# Revit family: FantiniCosmi_BIM_AP19981
name_source: partatom
category: Generic Models
units: mm (PartAtom-declared; Revit-internal decimal feet)

## family parameters
Always vertical = Yes
Can host rebar = No
Cut with Voids When Loaded = No
Part Type = Normal
Room Calculation Point = No
Round Connector Dimension = Use Diameter
Shared = No
Work Plane-Based = No

## types (1)
- Standard
    Default Elevation = 0 mm  [stored 0 ft]
    Description = ECOCOMFORT SAT 160 RF
    Designer = Carniti
    MAX dB(A) 1.5mt = 38
    POTENZA MAX ASSORBITA = 6.6 W
    Part Number = AP19981
    Tensione di alimentazione = 230V~ 50Hz
    UNITA’ = MASTER
    Velocità - Sleep = 15 m³/h
    Velocità Alta = 68 m³/h
    Velocità Bassa  = 28 m³/h
    Velocità Media = 48 m³/h
    Ø Tubo = 160mm

note: [stored X ft] marks values corroborated as IEEE doubles in the binary element streams (Revit-internal decimal feet)

## geometry (parser evidence)
native form markers: Sweep x3
no freeform markers — native parametric forms only
